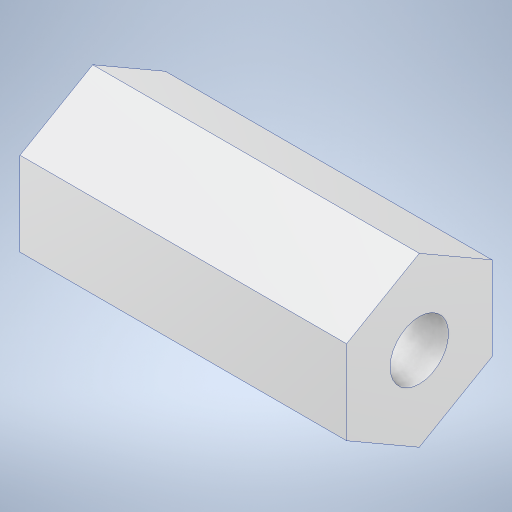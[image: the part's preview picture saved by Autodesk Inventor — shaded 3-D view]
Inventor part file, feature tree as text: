
AUTODESK INVENTOR PART (.ipt)
format: ipt  version: 2024 (Build 280153000, 153)  size: 204,288 bytes
history: native  units: in
note: dims shown in document units (in); Inventor stores cm internally (conversion verified against a paired STEP export)
features: extrude x1, sketch x1
ambient origin geometry x8: Origin, YZ Plane, XZ Plane, XY Plane, X Axis, Y Axis, Z Axis, Center Point
bodies: Solid1 (feature_tree)
feature tree (2):
  extrude  "Extrusion1"  Depth=0.5in
  sketch  "Sketch1"  dims[d0=0.201in d1=0.5in d2=1.123in d3=0.0in]
